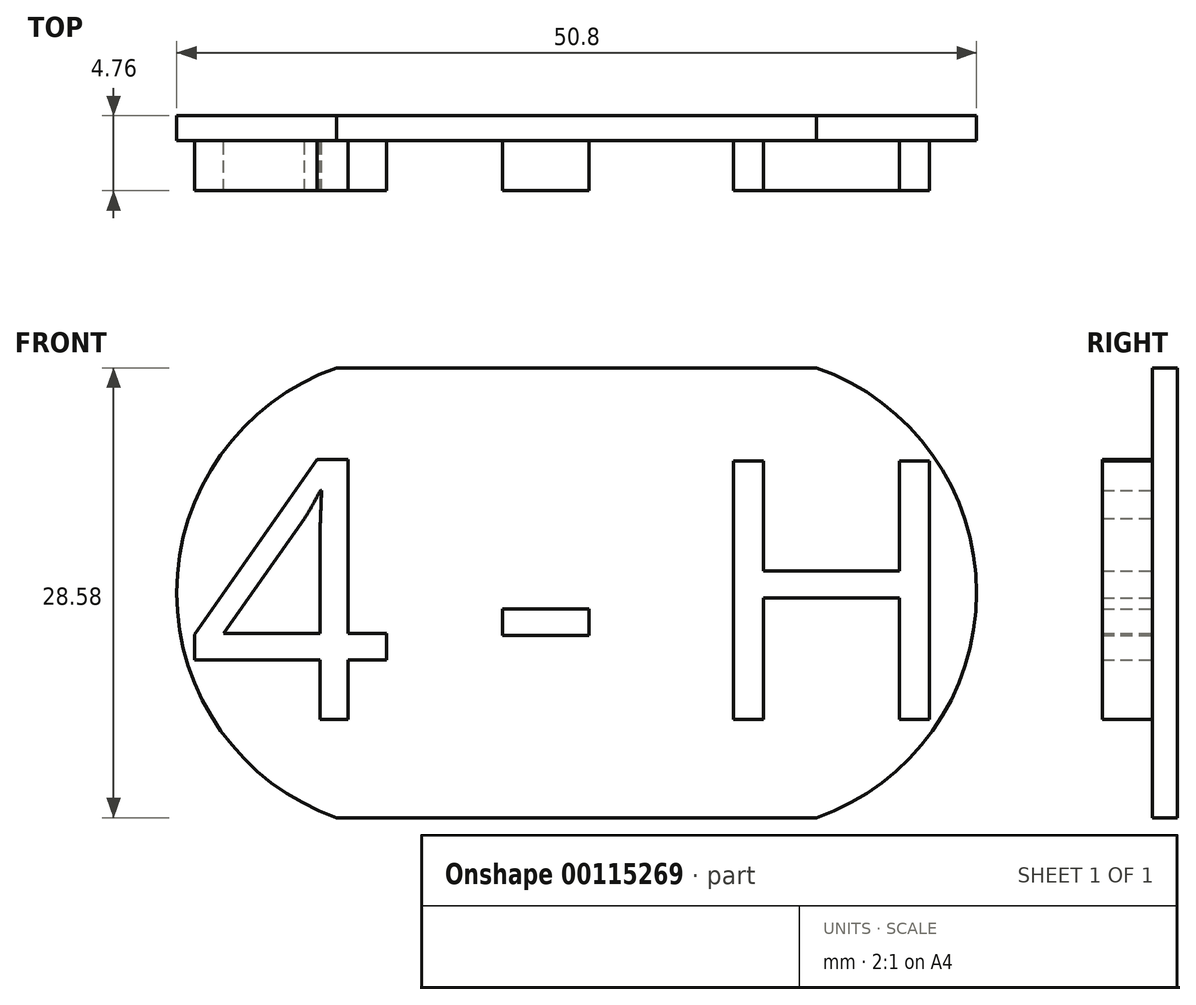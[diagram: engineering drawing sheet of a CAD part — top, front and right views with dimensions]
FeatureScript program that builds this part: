
annotation { "Feature Type Name" : "Feature", "Feature Type Description" : "" }
export const myFeature = defineFeature(function(context is Context, id is Id, definition is map)
    precondition{}
    {
        {
            var Q0;
            Q0=qCreatedBy(makeId("Front.planeOp"),FACE);
            var sketch = newSketch(context, id + "F0", { "sketchPlane" : qUnion([Q0])});
            skLineSegment(sketch, "E0.bottom", {"start": v(15.24, 14.29) * mm, "end": v(-15.24, 14.29) * mm});
            skLineSegment(sketch, "E0.top", {"start": v(15.24, -14.29) * mm, "end": v(-15.24, -14.29) * mm});
            skLineSegment(sketch, "E0.left", {"start": v(15.24, 14.29) * mm, "end": v(15.24, -14.29) * mm});
            skLineSegment(sketch, "E0.right", {"start": v(-15.24, 14.29) * mm, "end": v(-15.24, -14.29) * mm});
            skPoint(sketch, "E0.middle", {"position": v(0, 0) * mm});
            skArc(sketch, "E1", {"start": v(-15.24, 14.29) * mm, "mid": v(-25.4, 0) * mm, "end": v(-15.24, -14.29) * mm});
            skArc(sketch, "E2", {"start": v(15.24, -14.29) * mm, "mid": v(25.4, 0) * mm, "end": v(15.24, 14.29) * mm});
            skSolve(sketch);
        }
        {
            var Q0;
            Q0 = qSketchRegion(id + "F0", true);
            extrude(context, id + "F1", {"entities" : qUnion([Q0]), "depth" : 1.59 * mm});
        }
        {
            var Q0;
            Q0=makeQuery(id+"F1.opExtrude","CAP_FACE",FACE,{"disambiguationData":[OSD([sQuery(id+"F0.wireOp",EDGE,"E0.bottom"),sQuery(id+"F0.wireOp",EDGE,"E0.top"),sQuery(id+"F0.wireOp",EDGE,"E1"),sQuery(id+"F0.wireOp",EDGE,"E2")])],"isStart":false});
            var sketch = newSketch(context, id + "F2", { "sketchPlane" : qUnion([Q0])});
            skText(sketch, "E3", { "text": "4 - H", "fontName": "OpenSans-Regular.ttf"});
            const initialGuessF2  = {"E3": [-0.02476, -0.00803, 1, 0, 0.01654]};
            skSetInitialGuess(sketch, initialGuessF2);
            skSolve(sketch);
        }
        {
            var Q0;
            Q0 = qSketchRegion(id + "F2", true);
            extrude(context, id + "F3", {"entities" : qUnion([Q0]), "operationType" : NewBodyOperationType.ADD, "depth" : 3.17 * mm});
        }
    });
